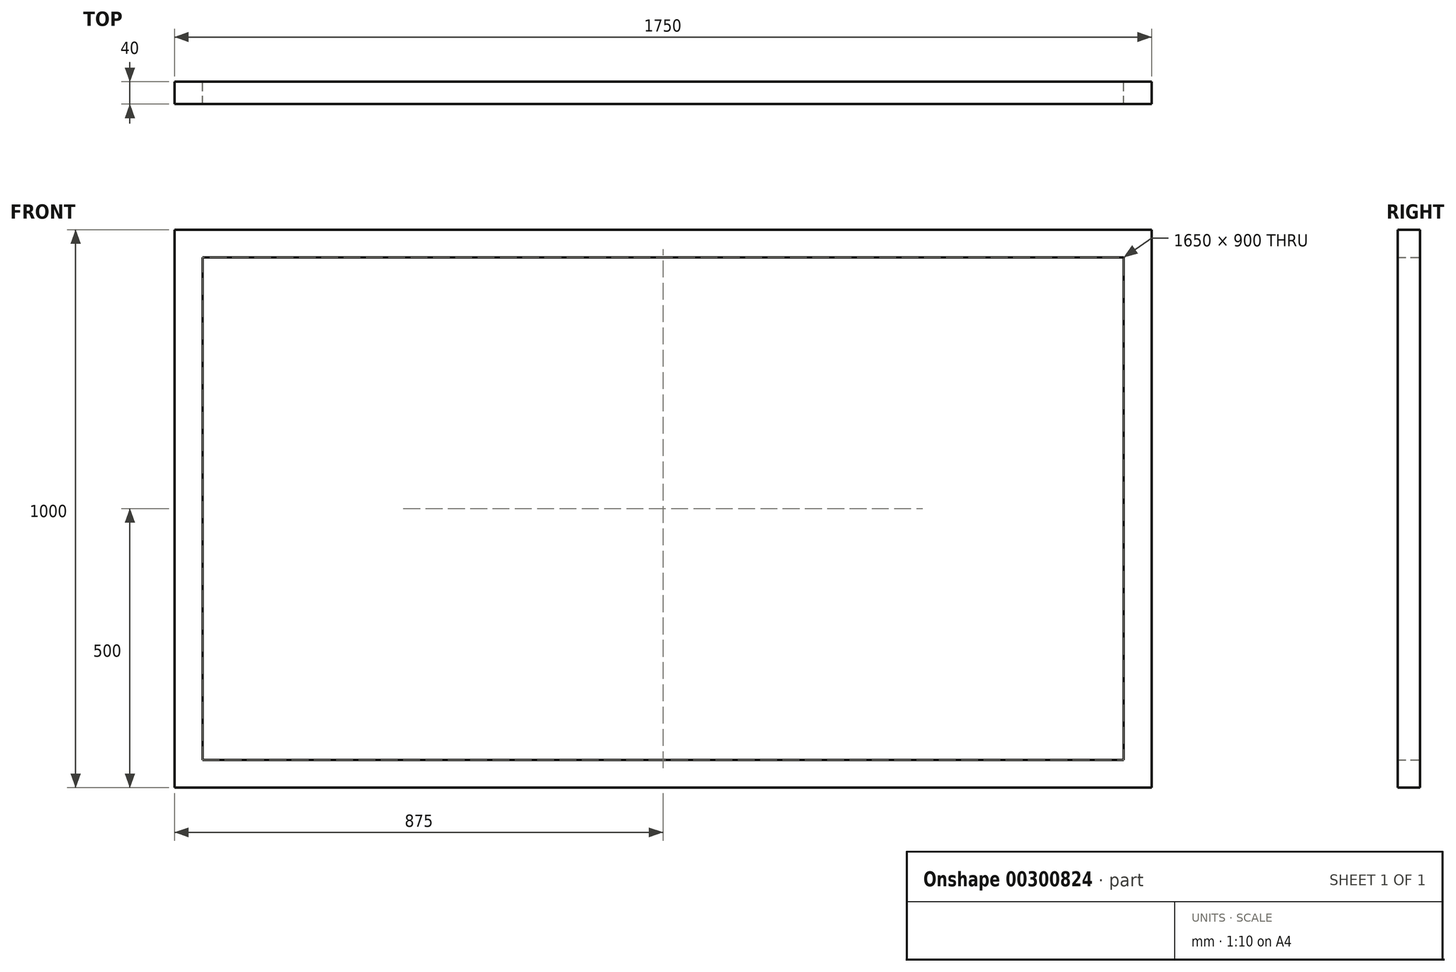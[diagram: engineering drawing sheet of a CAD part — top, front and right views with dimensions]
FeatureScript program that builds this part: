
annotation { "Feature Type Name" : "Feature", "Feature Type Description" : "" }
export const myFeature = defineFeature(function(context is Context, id is Id, definition is map)
    precondition{}
    {
        {
            var Q0;
            Q0=qCreatedBy(makeId("Front.planeOp"),FACE);
            var sketch = newSketch(context, id + "F0", { "sketchPlane" : qUnion([Q0])});
            skLineSegment(sketch, "E0.bottom", {"start": v(0, 0) * mm, "end": v(1750, 0) * mm});
            skLineSegment(sketch, "E0.top", {"start": v(0, -1000) * mm, "end": v(1750, -1000) * mm});
            skLineSegment(sketch, "E0.left", {"start": v(0, 0) * mm, "end": v(0, -1000) * mm});
            skLineSegment(sketch, "E0.right", {"start": v(1750, 0) * mm, "end": v(1750, -1000) * mm});
            skLineSegment(sketch, "E1.bottom", {"start": v(50, -50) * mm, "end": v(1700, -50) * mm});
            skLineSegment(sketch, "E1.top", {"start": v(50, -950) * mm, "end": v(1700, -950) * mm});
            skLineSegment(sketch, "E1.left", {"start": v(50, -50) * mm, "end": v(50, -950) * mm});
            skLineSegment(sketch, "E1.right", {"start": v(1700, -50) * mm, "end": v(1700, -950) * mm});
            skSolve(sketch);
        }
        {
            var Q0;
            Q0=makeQuery(id+"F0.imprint","IMPRINT",FACE,{"disambiguationData":[TD([[makeQuery(id+"F0.imprint","IMPRINT",EDGE,{"derivedFrom":sQuery(id+"F0.wireOp",EDGE,"E0.bottom")}),-1.0]])]});
            extrude(context, id + "F1", {"entities" : qUnion([Q0]), "depth" : 40 * mm});
        }
    });
